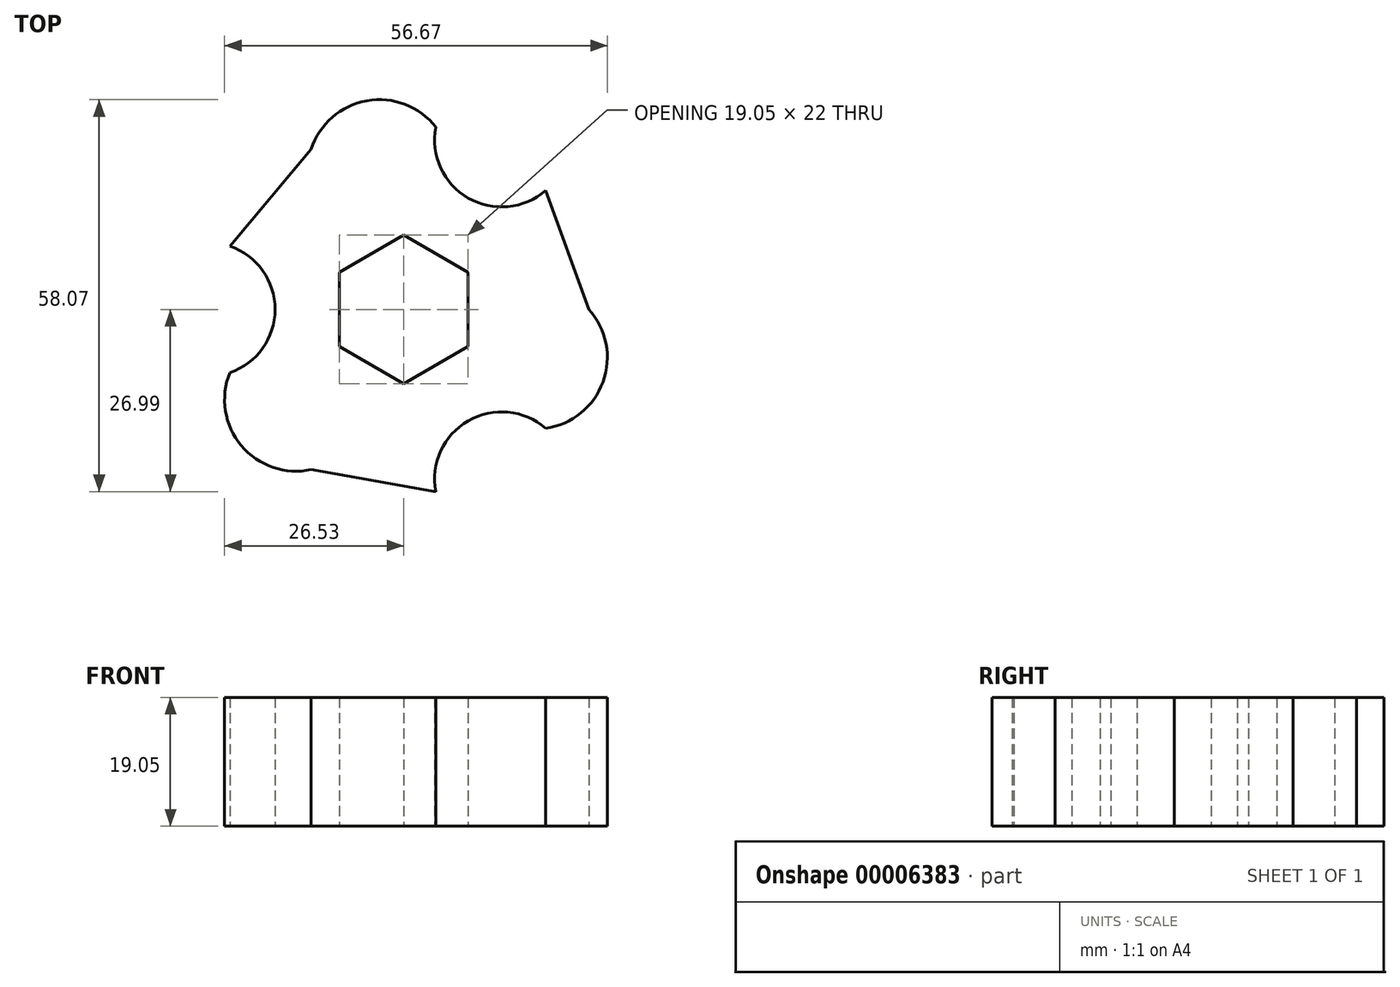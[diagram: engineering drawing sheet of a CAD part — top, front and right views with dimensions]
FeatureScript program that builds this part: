
annotation { "Feature Type Name" : "Feature", "Feature Type Description" : "" }
export const myFeature = defineFeature(function(context is Context, id is Id, definition is map)
    precondition{}
    {
        {
            var Q0;
            Q0=qCreatedBy(makeId("Top.planeOp"), FACE);
            var sketch = newSketch(context, id + "F0", { "sketchPlane" : qUnion([Q0])});
            skCircle(sketch, "E0.cCircle", {"center": v(0, 0) * mm, "radius": 9.53 * mm, "construction": true});
            skLineSegment(sketch, "E0.seed", {"start": v(9.53, -5.5) * mm, "end": v(9.53, 5.5) * mm});
            skLineSegment(sketch, "E0.pattern.0.1.0", {"start": v(9.53, 5.5) * mm, "end": v(0, 11) * mm});
            skLineSegment(sketch, "E0.pattern.0.2.0", {"start": v(0, 11) * mm, "end": v(-9.52, 5.5) * mm});
            skLineSegment(sketch, "E0.pattern.0.3.0", {"start": v(-9.53, 5.5) * mm, "end": v(-9.53, -5.5) * mm});
            skLineSegment(sketch, "E0.pattern.0.4.0", {"start": v(-9.53, -5.5) * mm, "end": v(0, -11) * mm});
            skLineSegment(sketch, "E0.pattern.0.5.0", {"start": v(0, -11) * mm, "end": v(9.53, -5.5) * mm});
            skPoint(sketch, "E0.midPoint", {"position": v(9.53, 0) * mm, "construction": true});
            skCircle(sketch, "E1.cCircle", {"center": v(0, 0) * mm, "radius": 27.4 * mm, "construction": true});
            skLineSegment(sketch, "E1.seed", {"start": v(21, -17.62) * mm, "end": v(27.4, 0) * mm});
            skLineSegment(sketch, "E1.pattern.0.1.0", {"start": v(27.4, 0) * mm, "end": v(21, 17.62) * mm});
            skLineSegment(sketch, "E1.pattern.0.3.0", {"start": v(4.76, 27) * mm, "end": v(-13.7, 23.74) * mm});
            skLineSegment(sketch, "E1.pattern.0.4.0", {"start": v(-13.7, 23.74) * mm, "end": v(-25.76, 9.37) * mm});
            skLineSegment(sketch, "E1.pattern.0.6.0", {"start": v(-25.76, -9.37) * mm, "end": v(-13.7, -23.74) * mm});
            skLineSegment(sketch, "E1.pattern.0.7.0", {"start": v(-13.7, -23.74) * mm, "end": v(4.76, -27) * mm});
            skArc(sketch, "E2", {"start": v(4.76, 27) * mm, "mid": v(9.53, 16.5) * mm, "end": v(21, 17.62) * mm});
            skArc(sketch, "E3", {"start": v(4.76, 27) * mm, "mid": v(-5.45, 30.92) * mm, "end": v(-13.7, 23.74) * mm});
            skArc(sketch, "E4.0.1.0", {"start": v(-25.76, -9.37) * mm, "mid": v(-19.06, 0) * mm, "end": v(-25.76, 9.37) * mm});
            skArc(sketch, "E4.1.1.0", {"start": v(-25.76, -9.37) * mm, "mid": v(-24.05, -20.18) * mm, "end": v(-13.7, -23.74) * mm});
            skArc(sketch, "E4.0.2.0", {"start": v(21, -17.62) * mm, "mid": v(9.53, -16.5) * mm, "end": v(4.76, -27) * mm});
            skArc(sketch, "E4.1.2.0", {"start": v(21, -17.62) * mm, "mid": v(29.5, -10.74) * mm, "end": v(27.4, 0) * mm});
            skLineSegment(sketch, "E4.anchor1", {"start": v(0, 0) * mm, "end": v(4.76, 27) * mm, "construction": true});
            skLineSegment(sketch, "E4.anchor2", {"start": v(0, 0) * mm, "end": v(21, -17.62) * mm, "construction": true});
            skSolve(sketch);
        }
        {
            var Q0;
            Q0 = qSketchRegion(id + "F0", true);
            extrude(context, id + "F1", {"entities" : qUnion([Q0]), "domain" : OperationDomain.MODEL, "flatOperationType" : FlatOperationType.REMOVE, "depth" : 19.05 * mm, "offsetDistance" : 25.4 * mm});
        }
    });
